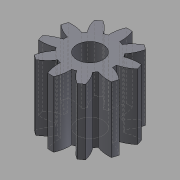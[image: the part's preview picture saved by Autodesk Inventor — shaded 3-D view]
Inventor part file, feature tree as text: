
AUTODESK INVENTOR PART (.ipt)
format: ipt  version: 2015 (Build 190159000, 159)  size: 199,168 bytes
history: native  units: mm (DEFAULTED — no unit token found)
features: plane x3, other x3, sketch x3, extrude x2
ambient origin geometry x8: Origin, YZ Plane, XZ Plane, XY Plane, X Axis, Y Axis, Z Axis, Center Point
bodies: Solid1 (feature_tree)
feature tree (11):
  extrude  "Extrusion1"  Depth=5.0mm TaperAngle=0.0deg
  plane  "Work Plane2"
  plane  "Work Plane8"
  plane  "Work Plane9"
  other  "Spur Gear"
  extrude  "Extrusion2"  Depth=10.0mm TaperAngle=0.0deg
  sketch  "Sketch1"  dims[d0=6.0mm d1=5.0mm d2=0.0mm]
  sketch  "Sketch2"  dims[d3=5.0mm d4=10.0mm d5=0.0mm]
  other  "Srf1"
  sketch  "Sketch3"  dims[d16=12.0mm d17=0.0mm d34=3.141593mm d39=0.0mm d41=0.0mm d43=12.0mm d46=12.0mm d47=0.0mm d48=0.0mm d49=2.0mm d50=10.0mm d51=0.0mm]
  other  "Pitch Diameter"
